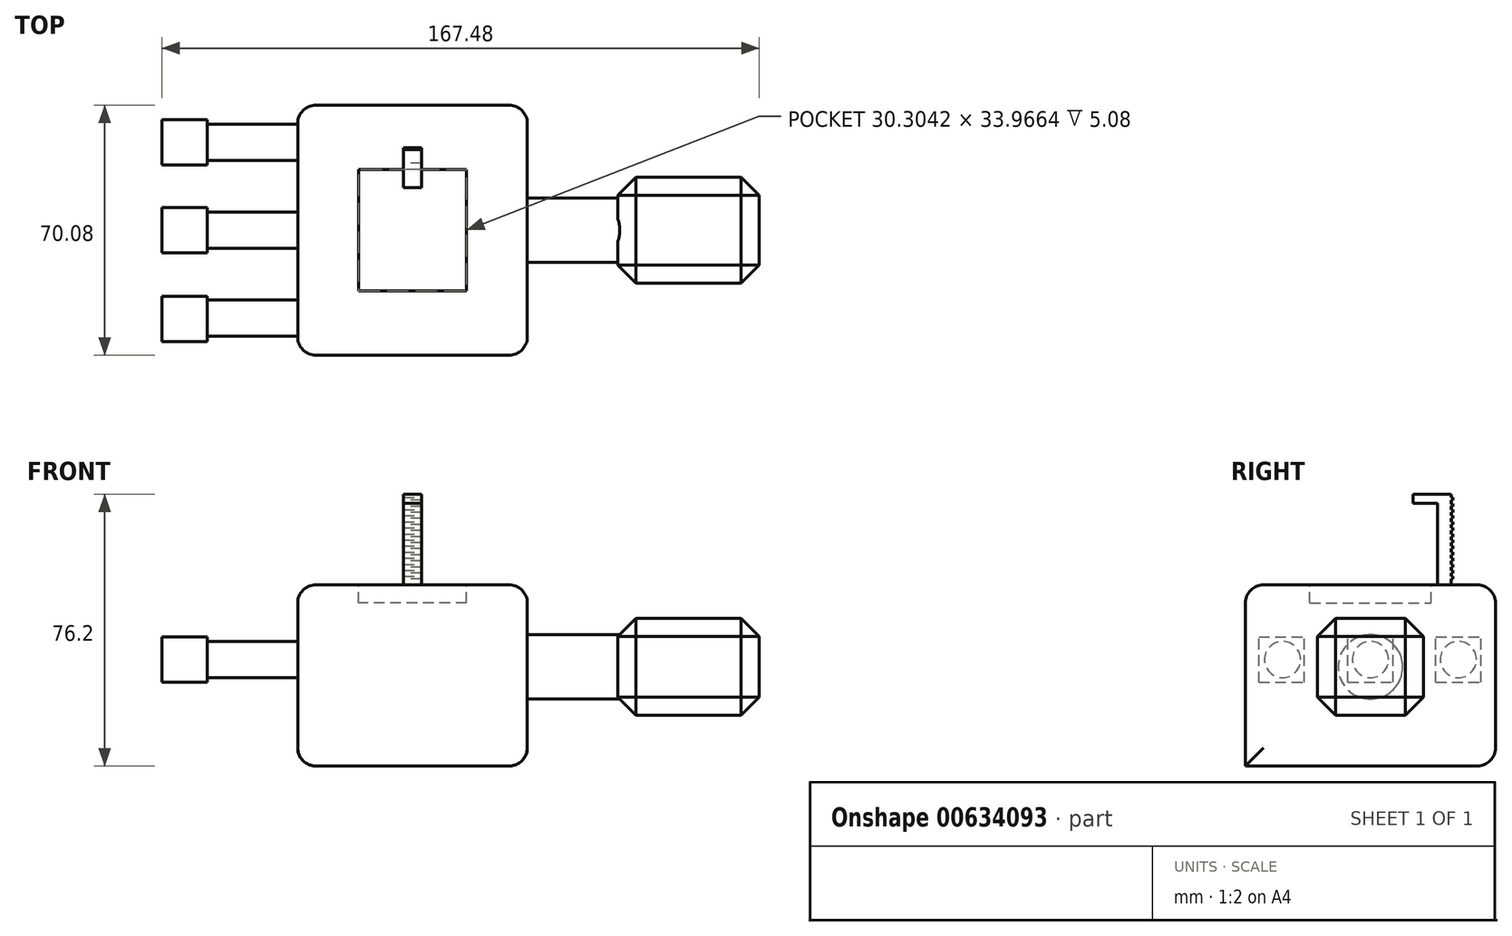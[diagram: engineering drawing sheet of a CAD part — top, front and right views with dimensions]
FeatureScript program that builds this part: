
annotation { "Feature Type Name" : "Feature", "Feature Type Description" : "" }
export const myFeature = defineFeature(function(context is Context, id is Id, definition is map)
    precondition{}
    {
        {
            var Q0;
            Q0=qCreatedBy(makeId("Top.planeOp"),FACE);
            var sketch = newSketch(context, id + "F0", { "sketchPlane" : qUnion([Q0])});
            skLineSegment(sketch, "E0.bottom", {"start": v(32.18, -35.04) * mm, "end": v(-32.18, -35.04) * mm});
            skLineSegment(sketch, "E0.top", {"start": v(32.18, 35.04) * mm, "end": v(-32.18, 35.04) * mm});
            skLineSegment(sketch, "E0.left", {"start": v(32.18, -35.04) * mm, "end": v(32.18, 35.04) * mm});
            skLineSegment(sketch, "E0.right", {"start": v(-32.18, -35.04) * mm, "end": v(-32.18, 35.04) * mm});
            skPoint(sketch, "E0.middle", {"position": v(0, 0) * mm});
            skSolve(sketch);
        }
        {
            var Q0;
            Q0 = qSketchRegion(id + "F0", true);
            extrude(context, id + "F1", {"entities" : qUnion([Q0]), "depth" : 50.8 * mm, "offsetDistance" : 25.4 * mm});
        }
        {
            var Q0;
            Q0=makeQuery(id+"F1.opExtrude","CAP_EDGE",EDGE,{"disambiguationData":[OSD([sQuery(id+"F0.wireOp",EDGE,"E0.left")])],"isStart":false});
            var Q1;
            Q1=makeQuery(id+"F1.opExtrude","SWEPT_EDGE",EDGE,{"disambiguationData":[OSD([sQuery(id+"F0.wireOp",EDGE,"E0.bottom"),sQuery(id+"F0.wireOp",EDGE,"E0.left")])]});
            var Q2;
            Q2=makeQuery(id+"F1.opExtrude","CAP_EDGE",EDGE,{"disambiguationData":[OSD([sQuery(id+"F0.wireOp",EDGE,"E0.bottom")])],"isStart":false});
            var Q3;
            Q3=makeQuery(id+"F1.opExtrude","SWEPT_EDGE",EDGE,{"disambiguationData":[OSD([sQuery(id+"F0.wireOp",EDGE,"E0.bottom"),sQuery(id+"F0.wireOp",EDGE,"E0.right")])]});
            var Q4;
            Q4=makeQuery(id+"F1.opExtrude","CAP_EDGE",EDGE,{"disambiguationData":[OSD([sQuery(id+"F0.wireOp",EDGE,"E0.right")])],"isStart":false});
            var Q5;
            Q5=makeQuery(id+"F1.opExtrude","SWEPT_FACE",FACE,{"disambiguationData":[OSD([sQuery(id+"F0.wireOp",EDGE,"E0.top")])]});
            var Q6;
            Q6=makeQuery(id+"F1.opExtrude","SWEPT_FACE",FACE,{"disambiguationData":[OSD([sQuery(id+"F0.wireOp",EDGE,"E0.right")])]});
            var Q7;
            Q7=makeQuery(id+"F1.opExtrude","SWEPT_FACE",FACE,{"disambiguationData":[OSD([sQuery(id+"F0.wireOp",EDGE,"E0.left")])]});
            fillet(context, id + "F2", {"entities" : qUnion([Q0, Q1, Q2, Q3, Q4, Q5, Q6, Q7]), "radius" : 5.08 * mm, "tangentPropagation" : true, "allowEdgeOverflow" : false});
        }
        {
            var Q0;
            Q0=makeQuery(id+"F1.opExtrude","CAP_FACE",FACE,{"disambiguationData":[OSD([sQuery(id+"F0.wireOp",EDGE,"E0.bottom"),sQuery(id+"F0.wireOp",EDGE,"E0.top"),sQuery(id+"F0.wireOp",EDGE,"E0.left"),sQuery(id+"F0.wireOp",EDGE,"E0.right")])],"isStart":false});
            var sketch = newSketch(context, id + "F3", { "sketchPlane" : qUnion([Q0])});
            skLineSegment(sketch, "E1.bottom", {"start": v(15.15, -16.98) * mm, "end": v(-15.15, -16.98) * mm});
            skLineSegment(sketch, "E1.top", {"start": v(15.15, 16.98) * mm, "end": v(-15.15, 16.98) * mm});
            skLineSegment(sketch, "E1.left", {"start": v(15.15, -16.98) * mm, "end": v(15.15, 16.98) * mm});
            skLineSegment(sketch, "E1.right", {"start": v(-15.15, -16.98) * mm, "end": v(-15.15, 16.98) * mm});
            skPoint(sketch, "E1.middle", {"position": v(0, 0) * mm});
            skSolve(sketch);
        }
        {
            var Q0;
            Q0 = qSketchRegion(id + "F3", true);
            extrude(context, id + "F4", {"entities" : qUnion([Q0]), "operationType" : NewBodyOperationType.REMOVE, "oppositeDirection" : true, "depth" : 5.08 * mm, "offsetDistance" : 25.4 * mm});
        }
        {
            var Q0;
            Q0=makeQuery(id+"F1.opExtrude","CAP_FACE",FACE,{"disambiguationData":[OSD([sQuery(id+"F0.wireOp",EDGE,"E0.bottom"),sQuery(id+"F0.wireOp",EDGE,"E0.top"),sQuery(id+"F0.wireOp",EDGE,"E0.left"),sQuery(id+"F0.wireOp",EDGE,"E0.right")])],"isStart":false});
            var sketch = newSketch(context, id + "F5", { "sketchPlane" : qUnion([Q0])});
            skLineSegment(sketch, "E2.bottom", {"start": v(2.5, 18.83) * mm, "end": v(-2.5, 18.83) * mm});
            skLineSegment(sketch, "E2.top", {"start": v(2.5, 22.6) * mm, "end": v(-2.5, 22.6) * mm});
            skLineSegment(sketch, "E2.left", {"start": v(2.5, 18.83) * mm, "end": v(2.5, 22.6) * mm});
            skLineSegment(sketch, "E2.right", {"start": v(-2.5, 18.83) * mm, "end": v(-2.5, 22.6) * mm});
            skPoint(sketch, "E2.middle", {"position": v(0, 20.72) * mm});
            skSolve(sketch);
        }
        {
            var Q0;
            Q0 = qSketchRegion(id + "F5", true);
            extrude(context, id + "F6", {"entities" : qUnion([Q0]), "operationType" : NewBodyOperationType.ADD, "depth" : 25.4 * mm, "offsetDistance" : 25.4 * mm});
        }
        {
            var Q0;
            Q0=makeQuery(id+"F6.opExtrude","SWEPT_FACE",FACE,{"disambiguationData":[OSD([sQuery(id+"F5.wireOp",EDGE,"E2.bottom")])]});
            var sketch = newSketch(context, id + "F7", { "sketchPlane" : qUnion([Q0])});
            skLineSegment(sketch, "E3.bottom", {"start": v(2.5, 73.66) * mm, "end": v(-2.5, 73.66) * mm});
            skLineSegment(sketch, "E3.top", {"start": v(2.5, 76.2) * mm, "end": v(-2.5, 76.2) * mm});
            skLineSegment(sketch, "E3.left", {"start": v(2.5, 73.66) * mm, "end": v(2.5, 76.2) * mm});
            skLineSegment(sketch, "E3.right", {"start": v(-2.5, 73.66) * mm, "end": v(-2.5, 76.2) * mm});
            skPoint(sketch, "E3.middle", {"position": v(0, 74.93) * mm});
            skSolve(sketch);
        }
        {
            var Q0;
            Q0 = qSketchRegion(id + "F7", true);
            extrude(context, id + "F8", {"entities" : qUnion([Q0]), "operationType" : NewBodyOperationType.ADD, "depth" : 6.86 * mm, "offsetDistance" : 25.4 * mm});
        }
        {
            var Q0;
            Q0=makeQuery(id+"F6.opExtrude","SWEPT_FACE",FACE,{"disambiguationData":[OSD([sQuery(id+"F5.wireOp",EDGE,"E2.top")])]});
            var sketch = newSketch(context, id + "F9", { "sketchPlane" : qUnion([Q0])});
            skLineSegment(sketch, "E4", {"start": v(-2.5, 52.4) * mm, "end": v(2.5, 52.4) * mm});
            skLineSegment(sketch, "E5", {"start": v(2.5, 52.4) * mm, "end": v(2.5, 53.16) * mm});
            skLineSegment(sketch, "E6", {"start": v(2.5, 53.16) * mm, "end": v(-2.5, 53.16) * mm});
            skLineSegment(sketch, "E7", {"start": v(-2.5, 53.16) * mm, "end": v(-2.5, 52.4) * mm});
            skLineSegment(sketch, "E8", {"start": v(2.5, 54.1) * mm, "end": v(2.5, 54.86) * mm});
            skLineSegment(sketch, "E9", {"start": v(2.5, 54.86) * mm, "end": v(-2.5, 54.86) * mm});
            skLineSegment(sketch, "E10", {"start": v(-2.5, 54.86) * mm, "end": v(-2.5, 54.1) * mm});
            skLineSegment(sketch, "E11", {"start": v(-2.5, 54.1) * mm, "end": v(2.5, 54.1) * mm});
            skLineSegment(sketch, "E12", {"start": v(2.5, 55.8) * mm, "end": v(2.5, 56.56) * mm});
            skLineSegment(sketch, "E13", {"start": v(2.5, 56.56) * mm, "end": v(-2.5, 56.56) * mm});
            skLineSegment(sketch, "E14", {"start": v(-2.5, 56.56) * mm, "end": v(-2.5, 55.8) * mm});
            skLineSegment(sketch, "E15", {"start": v(-2.5, 55.8) * mm, "end": v(2.5, 55.8) * mm});
            skLineSegment(sketch, "E16", {"start": v(2.5, 57.5) * mm, "end": v(2.5, 58.26) * mm});
            skLineSegment(sketch, "E17", {"start": v(2.5, 58.26) * mm, "end": v(-2.5, 58.26) * mm});
            skLineSegment(sketch, "E18", {"start": v(-2.5, 58.26) * mm, "end": v(-2.5, 57.5) * mm});
            skLineSegment(sketch, "E19", {"start": v(-2.5, 57.5) * mm, "end": v(2.5, 57.5) * mm});
            skLineSegment(sketch, "E20", {"start": v(2.49, 59.2) * mm, "end": v(2.49, 59.96) * mm});
            skLineSegment(sketch, "E21", {"start": v(2.49, 59.96) * mm, "end": v(-2.5, 59.96) * mm});
            skLineSegment(sketch, "E22", {"start": v(-2.5, 59.96) * mm, "end": v(-2.5, 59.2) * mm});
            skLineSegment(sketch, "E23", {"start": v(-2.5, 59.2) * mm, "end": v(2.49, 59.2) * mm});
            skLineSegment(sketch, "E24", {"start": v(2.5, 60.9) * mm, "end": v(2.5, 61.66) * mm});
            skLineSegment(sketch, "E25", {"start": v(2.5, 61.66) * mm, "end": v(-2.5, 61.66) * mm});
            skLineSegment(sketch, "E26", {"start": v(-2.5, 61.66) * mm, "end": v(-2.5, 60.9) * mm});
            skLineSegment(sketch, "E27", {"start": v(-2.5, 60.9) * mm, "end": v(2.5, 60.9) * mm});
            skLineSegment(sketch, "E28", {"start": v(2.5, 62.6) * mm, "end": v(2.5, 63.37) * mm});
            skLineSegment(sketch, "E29", {"start": v(2.5, 63.37) * mm, "end": v(-2.5, 63.37) * mm});
            skLineSegment(sketch, "E30", {"start": v(-2.5, 63.37) * mm, "end": v(-2.5, 62.6) * mm});
            skLineSegment(sketch, "E31", {"start": v(-2.5, 62.6) * mm, "end": v(2.5, 62.6) * mm});
            skLineSegment(sketch, "E32", {"start": v(2.5, 64.3) * mm, "end": v(2.5, 65.07) * mm});
            skLineSegment(sketch, "E33", {"start": v(2.5, 65.07) * mm, "end": v(-2.5, 65.07) * mm});
            skLineSegment(sketch, "E34", {"start": v(-2.5, 65.07) * mm, "end": v(-2.5, 64.3) * mm});
            skLineSegment(sketch, "E35", {"start": v(-2.5, 64.3) * mm, "end": v(2.5, 64.3) * mm});
            skLineSegment(sketch, "E36", {"start": v(2.5, 66) * mm, "end": v(2.5, 66.77) * mm});
            skLineSegment(sketch, "E37", {"start": v(2.5, 66.77) * mm, "end": v(-2.5, 66.77) * mm});
            skLineSegment(sketch, "E38", {"start": v(-2.5, 66.77) * mm, "end": v(-2.5, 66) * mm});
            skLineSegment(sketch, "E39", {"start": v(-2.5, 66) * mm, "end": v(2.5, 66) * mm});
            skLineSegment(sketch, "E40", {"start": v(2.5, 67.7) * mm, "end": v(2.5, 68.47) * mm});
            skLineSegment(sketch, "E41", {"start": v(2.5, 68.47) * mm, "end": v(-2.5, 68.47) * mm});
            skLineSegment(sketch, "E42", {"start": v(-2.5, 68.47) * mm, "end": v(-2.5, 67.7) * mm});
            skLineSegment(sketch, "E43", {"start": v(-2.5, 67.7) * mm, "end": v(2.5, 67.7) * mm});
            skLineSegment(sketch, "E44", {"start": v(2.5, 69.41) * mm, "end": v(2.5, 70.17) * mm});
            skLineSegment(sketch, "E45", {"start": v(2.5, 70.17) * mm, "end": v(-2.5, 70.17) * mm});
            skLineSegment(sketch, "E46", {"start": v(-2.5, 70.17) * mm, "end": v(-2.5, 69.41) * mm});
            skLineSegment(sketch, "E47", {"start": v(-2.5, 69.41) * mm, "end": v(2.5, 69.41) * mm});
            skLineSegment(sketch, "E48", {"start": v(2.5, 71.11) * mm, "end": v(2.5, 71.87) * mm});
            skLineSegment(sketch, "E49", {"start": v(2.5, 71.87) * mm, "end": v(-2.5, 71.87) * mm});
            skLineSegment(sketch, "E50", {"start": v(-2.5, 71.87) * mm, "end": v(-2.5, 71.11) * mm});
            skLineSegment(sketch, "E51", {"start": v(-2.5, 71.11) * mm, "end": v(2.5, 71.11) * mm});
            skLineSegment(sketch, "E52", {"start": v(2.48, 72.81) * mm, "end": v(2.48, 73.58) * mm});
            skLineSegment(sketch, "E53", {"start": v(2.48, 73.58) * mm, "end": v(-2.5, 73.58) * mm});
            skLineSegment(sketch, "E54", {"start": v(-2.5, 73.58) * mm, "end": v(-2.5, 72.81) * mm});
            skLineSegment(sketch, "E55", {"start": v(-2.5, 72.81) * mm, "end": v(2.48, 72.81) * mm});
            skLineSegment(sketch, "E56", {"start": v(2.5, 74.52) * mm, "end": v(2.5, 75.28) * mm});
            skLineSegment(sketch, "E57", {"start": v(2.5, 75.28) * mm, "end": v(-2.5, 75.28) * mm});
            skLineSegment(sketch, "E58", {"start": v(-2.5, 75.28) * mm, "end": v(-2.5, 74.52) * mm});
            skLineSegment(sketch, "E59", {"start": v(-2.5, 74.52) * mm, "end": v(2.5, 74.52) * mm});
            skSolve(sketch);
        }
        {
            var Q0;
            Q0 = qSketchRegion(id + "F9", true);
            extrude(context, id + "F10", {"entities" : qUnion([Q0]), "operationType" : NewBodyOperationType.ADD, "depth" : 0.5 * mm, "offsetDistance" : 25.4 * mm});
        }
        {
            var Q0;
            Q0=makeQuery(id+"F1.opExtrude","SWEPT_FACE",FACE,{"disambiguationData":[OSD([sQuery(id+"F0.wireOp",EDGE,"E0.left")])]});
            var sketch = newSketch(context, id + "F11", { "sketchPlane" : qUnion([Q0])});
            skCircle(sketch, "E60", {"center": v(0, 27.79) * mm, "radius": 9.02 * mm});
            skSolve(sketch);
        }
        {
            var Q0;
            Q0 = qSketchRegion(id + "F11", true);
            extrude(context, id + "F12", {"entities" : qUnion([Q0]), "operationType" : NewBodyOperationType.ADD, "depth" : 25.4 * mm, "offsetDistance" : 25.4 * mm});
        }
        {
            var Q0;
            Q0=makeQuery(id+"F12.opExtrude","CAP_FACE",FACE,{"disambiguationData":[OSD([sQuery(id+"F11.wireOp",EDGE,"E60")])],"isStart":false});
            var sketch = newSketch(context, id + "F13", { "sketchPlane" : qUnion([Q0])});
            skLineSegment(sketch, "E61.bottom", {"start": v(14.9, 14.21) * mm, "end": v(-14.9, 14.21) * mm});
            skLineSegment(sketch, "E61.top", {"start": v(14.9, 41.36) * mm, "end": v(-14.9, 41.36) * mm});
            skLineSegment(sketch, "E61.left", {"start": v(14.9, 14.21) * mm, "end": v(14.9, 41.36) * mm});
            skLineSegment(sketch, "E61.right", {"start": v(-14.9, 14.21) * mm, "end": v(-14.9, 41.36) * mm});
            skPoint(sketch, "E61.middle", {"position": v(0, 27.79) * mm});
            skSolve(sketch);
        }
        {
            var Q0;
            Q0 = qSketchRegion(id + "F13", true);
            extrude(context, id + "F14", {"entities" : qUnion([Q0]), "operationType" : NewBodyOperationType.ADD, "depth" : 39.62 * mm, "offsetDistance" : 25.4 * mm});
        }
        {
            var Q0;
            Q0=makeQuery(id+"F14.opExtrude","SWEPT_EDGE",EDGE,{"disambiguationData":[OSD([sQuery(id+"F13.wireOp",EDGE,"E61.top"),sQuery(id+"F13.wireOp",EDGE,"E61.left")])]});
            var Q1;
            Q1=makeQuery(id+"F14.opExtrude","CAP_EDGE",EDGE,{"disambiguationData":[OSD([sQuery(id+"F13.wireOp",EDGE,"E61.left")])],"isStart":true});
            var Q2;
            Q2=makeQuery(id+"F14.opExtrude","CAP_EDGE",EDGE,{"disambiguationData":[OSD([sQuery(id+"F13.wireOp",EDGE,"E61.left")])],"isStart":false});
            var Q3;
            Q3=makeQuery(id+"F14.opExtrude","CAP_EDGE",EDGE,{"disambiguationData":[OSD([sQuery(id+"F13.wireOp",EDGE,"E61.right")])],"isStart":false});
            var Q4;
            Q4=makeQuery(id+"F14.opExtrude","CAP_EDGE",EDGE,{"disambiguationData":[OSD([sQuery(id+"F13.wireOp",EDGE,"E61.bottom")])],"isStart":false});
            var Q5;
            Q5=makeQuery(id+"F14.opExtrude","CAP_EDGE",EDGE,{"disambiguationData":[OSD([sQuery(id+"F13.wireOp",EDGE,"E61.top")])],"isStart":false});
            var Q6;
            Q6=makeQuery(id+"F14.opExtrude","SWEPT_EDGE",EDGE,{"disambiguationData":[OSD([sQuery(id+"F13.wireOp",EDGE,"E61.bottom"),sQuery(id+"F13.wireOp",EDGE,"E61.right")])]});
            var Q7;
            Q7=makeQuery(id+"F14.opExtrude","SWEPT_EDGE",EDGE,{"disambiguationData":[OSD([sQuery(id+"F13.wireOp",EDGE,"E61.top"),sQuery(id+"F13.wireOp",EDGE,"E61.right")])]});
            var Q8;
            Q8=makeQuery(id+"F14.opExtrude","CAP_EDGE",EDGE,{"disambiguationData":[OSD([sQuery(id+"F13.wireOp",EDGE,"E61.top")])],"isStart":true});
            var Q9;
            Q9=makeQuery(id+"F14.opExtrude","CAP_EDGE",EDGE,{"disambiguationData":[OSD([sQuery(id+"F13.wireOp",EDGE,"E61.right")])],"isStart":true});
            var Q10;
            Q10=makeQuery(id+"F14.opExtrude","CAP_EDGE",EDGE,{"disambiguationData":[OSD([sQuery(id+"F13.wireOp",EDGE,"E61.bottom")])],"isStart":true});
            var Q11;
            Q11=makeQuery(id+"F14.opExtrude","SWEPT_FACE",FACE,{"disambiguationData":[OSD([sQuery(id+"F13.wireOp",EDGE,"E61.bottom")])]});
            chamfer(context, id + "F15", {"entities" : qUnion([Q0, Q1, Q2, Q3, Q4, Q5, Q6, Q7, Q8, Q9, Q10, Q11]), "width" : 5.08 * mm, "tangentPropagation" : true});
        }
        {
            var Q0;
            Q0=makeQuery(id+"F1.opExtrude","SWEPT_FACE",FACE,{"disambiguationData":[OSD([sQuery(id+"F0.wireOp",EDGE,"E0.right")])]});
            var sketch = newSketch(context, id + "F16", { "sketchPlane" : qUnion([Q0])});
            skCircle(sketch, "E62", {"center": v(-24.64, 29.84) * mm, "radius": 5.08 * mm});
            skCircle(sketch, "E63", {"center": v(0, 29.84) * mm, "radius": 5.08 * mm});
            skCircle(sketch, "E64", {"center": v(24.64, 29.84) * mm, "radius": 5.08 * mm});
            skSolve(sketch);
        }
        {
            var Q0;
            Q0 = qSketchRegion(id + "F16", true);
            extrude(context, id + "F17", {"entities" : qUnion([Q0]), "operationType" : NewBodyOperationType.ADD, "depth" : 25.4 * mm, "offsetDistance" : 25.4 * mm});
        }
        {
            var Q0;
            Q0=makeQuery(id+"F17.opExtrude","CAP_FACE",FACE,{"disambiguationData":[OSD([sQuery(id+"F16.wireOp",EDGE,"E62")])],"isStart":false});
            var sketch = newSketch(context, id + "F18", { "sketchPlane" : qUnion([Q0])});
            skLineSegment(sketch, "E65.bottom", {"start": v(-18.29, 23.49) * mm, "end": v(-30.99, 23.49) * mm});
            skLineSegment(sketch, "E65.top", {"start": v(-18.29, 36.19) * mm, "end": v(-30.99, 36.19) * mm});
            skLineSegment(sketch, "E65.left", {"start": v(-18.29, 23.49) * mm, "end": v(-18.29, 36.19) * mm});
            skLineSegment(sketch, "E65.right", {"start": v(-30.99, 23.49) * mm, "end": v(-30.99, 36.19) * mm});
            skPoint(sketch, "E65.middle", {"position": v(-24.64, 29.84) * mm});
            skLineSegment(sketch, "E66.bottom", {"start": v(6.32, 23.49) * mm, "end": v(-6.38, 23.49) * mm});
            skLineSegment(sketch, "E66.top", {"start": v(6.32, 36.19) * mm, "end": v(-6.38, 36.19) * mm});
            skLineSegment(sketch, "E66.left", {"start": v(6.32, 23.49) * mm, "end": v(6.32, 36.19) * mm});
            skLineSegment(sketch, "E66.right", {"start": v(-6.38, 23.49) * mm, "end": v(-6.38, 36.19) * mm});
            skPoint(sketch, "E66.middle", {"position": v(-0.03, 29.84) * mm});
            skLineSegment(sketch, "E67.bottom", {"start": v(31.3, 23.48) * mm, "end": v(18.6, 23.48) * mm});
            skLineSegment(sketch, "E67.top", {"start": v(31.3, 36.18) * mm, "end": v(18.6, 36.18) * mm});
            skLineSegment(sketch, "E67.left", {"start": v(31.3, 23.48) * mm, "end": v(31.3, 36.18) * mm});
            skLineSegment(sketch, "E67.right", {"start": v(18.6, 23.48) * mm, "end": v(18.6, 36.18) * mm});
            skPoint(sketch, "E67.middle", {"position": v(24.94, 29.83) * mm});
            skSolve(sketch);
        }
        {
            var Q0;
            Q0 = qSketchRegion(id + "F18", true);
            extrude(context, id + "F19", {"entities" : qUnion([Q0]), "operationType" : NewBodyOperationType.ADD, "depth" : 12.7 * mm, "offsetDistance" : 25.4 * mm});
        }
    });
